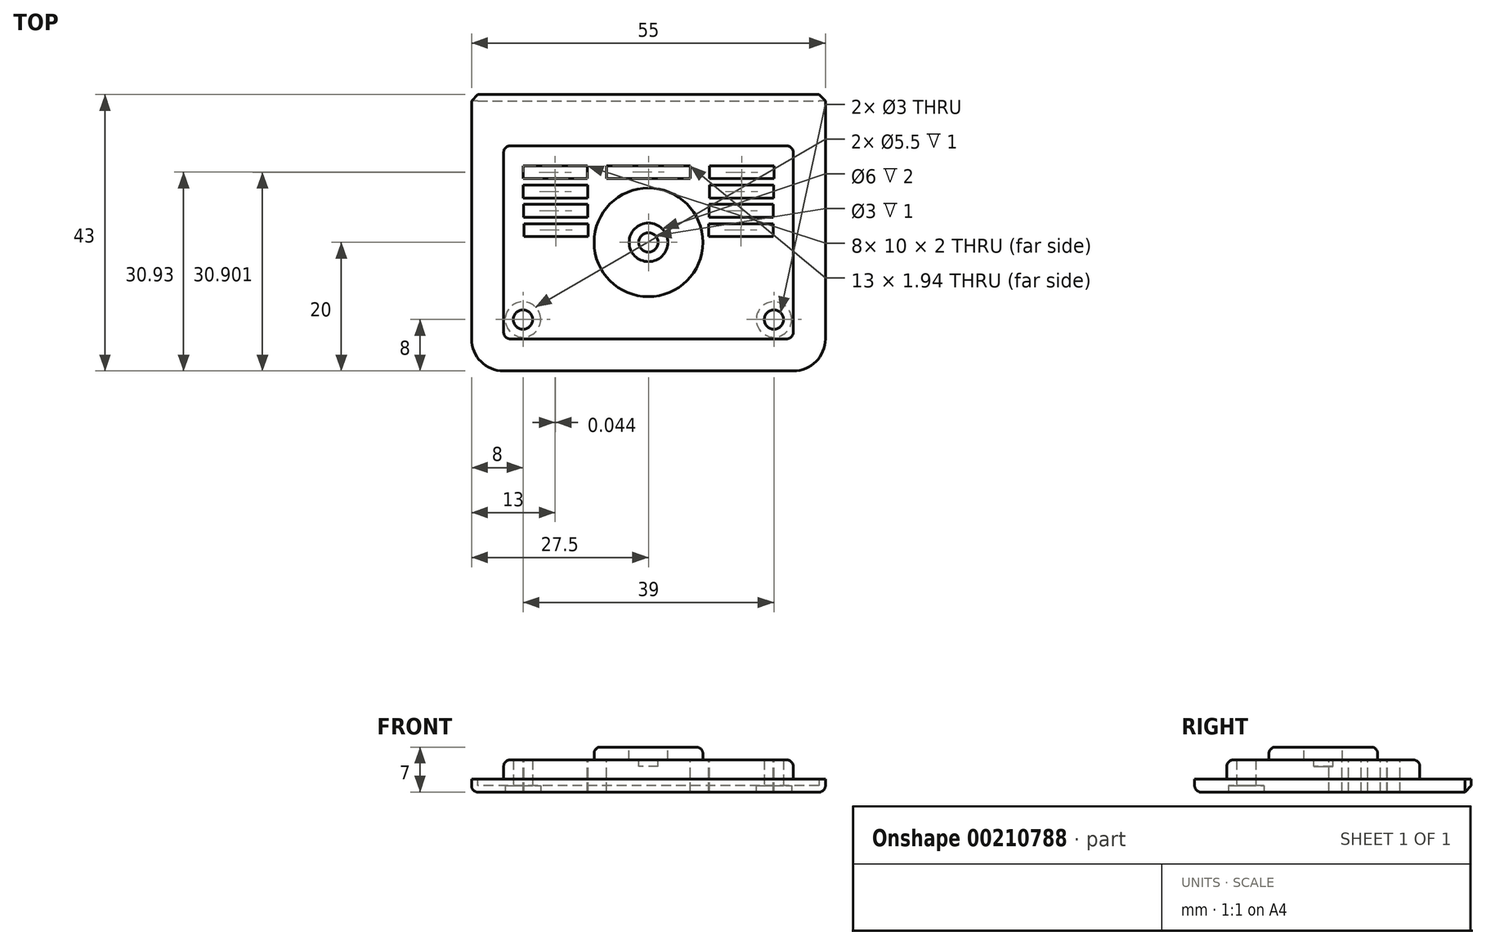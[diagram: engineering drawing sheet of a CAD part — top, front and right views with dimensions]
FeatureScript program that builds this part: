
annotation { "Feature Type Name" : "Feature", "Feature Type Description" : "" }
export const myFeature = defineFeature(function(context is Context, id is Id, definition is map)
    precondition{}
    {
        {
            var Q0;
            Q0=qCreatedBy(makeId("Top.planeOp"),FACE);
            var sketch = newSketch(context, id + "F0", { "sketchPlane" : qUnion([Q0])});
            skLineSegment(sketch, "E0.bottom", {"start": v(27.5, -20) * mm, "end": v(-27.5, -20) * mm});
            skLineSegment(sketch, "E0.top", {"start": v(27.5, 20) * mm, "end": v(-27.5, 20) * mm});
            skLineSegment(sketch, "E0.left", {"start": v(27.5, -20) * mm, "end": v(27.5, 20) * mm});
            skLineSegment(sketch, "E0.right", {"start": v(-27.5, -20) * mm, "end": v(-27.5, 20) * mm});
            skPoint(sketch, "E0.middle", {"position": v(0, 0) * mm});
            skSolve(sketch);
        }
        {
            var Q0;
            Q0 = qSketchRegion(id + "F0", true);
            extrude(context, id + "F1", {"entities" : qUnion([Q0]), "oppositeDirection" : true, "depth" : 2 * mm});
        }
        {
            var Q0;
            Q0=makeQuery(id+"F1.opExtrude","CAP_FACE",FACE,{"disambiguationData":[OSD([sQuery(id+"F0.wireOp",EDGE,"E0.bottom"),sQuery(id+"F0.wireOp",EDGE,"E0.top"),sQuery(id+"F0.wireOp",EDGE,"E0.left"),sQuery(id+"F0.wireOp",EDGE,"E0.right")])],"isStart":true});
            var sketch = newSketch(context, id + "F2", { "sketchPlane" : qUnion([Q0])});
            skLineSegment(sketch, "E1.bottom", {"start": v(-22.5, 15) * mm, "end": v(22.5, 15) * mm});
            skLineSegment(sketch, "E1.top", {"start": v(-22.5, -15) * mm, "end": v(22.5, -15) * mm});
            skLineSegment(sketch, "E1.left", {"start": v(-22.5, 15) * mm, "end": v(-22.5, -15) * mm});
            skLineSegment(sketch, "E1.right", {"start": v(22.5, 15) * mm, "end": v(22.5, -15) * mm});
            skSolve(sketch);
        }
        {
            var Q0;
            Q0 = qSketchRegion(id + "F2", true);
            extrude(context, id + "F3", {"entities" : qUnion([Q0]), "operationType" : NewBodyOperationType.ADD, "depth" : 3 * mm});
        }
        {
            var Q0;
            Q0=makeQuery(id+"F1.opExtrude","CAP_FACE",FACE,{"disambiguationData":[OSD([sQuery(id+"F0.wireOp",EDGE,"E0.bottom"),sQuery(id+"F0.wireOp",EDGE,"E0.top"),sQuery(id+"F0.wireOp",EDGE,"E0.left"),sQuery(id+"F0.wireOp",EDGE,"E0.right")])],"isStart":false});
            var sketch = newSketch(context, id + "F4", { "sketchPlane" : qUnion([Q0])});
            skCircle(sketch, "E2", {"center": v(19.5, 12) * mm, "radius": 1.5 * mm});
            skCircle(sketch, "E3", {"center": v(-19.5, 12) * mm, "radius": 1.5 * mm});
            skSolve(sketch);
        }
        {
            var Q0;
            Q0 = qSketchRegion(id + "F4", true);
            extrude(context, id + "F5", {"entities" : qUnion([Q0]), "operationType" : NewBodyOperationType.REMOVE, "oppositeDirection" : true, "depth" : 25 * mm});
        }
        {
            var Q0;
            Q0=makeQuery(id+"F3.opExtrude","CAP_FACE",FACE,{"disambiguationData":[OSD([sQuery(id+"F2.wireOp",EDGE,"E1.bottom"),sQuery(id+"F2.wireOp",EDGE,"E1.top"),sQuery(id+"F2.wireOp",EDGE,"E1.left"),sQuery(id+"F2.wireOp",EDGE,"E1.right")])],"isStart":false});
            var sketch = newSketch(context, id + "F6", { "sketchPlane" : qUnion([Q0])});
            skCircle(sketch, "E4", {"center": v(0, 0) * mm, "radius": 8.45 * mm});
            skSolve(sketch);
        }
        {
            var Q0;
            Q0=makeQuery(id+"F6.imprint","IMPRINT",FACE,{"disambiguationData":[TD([[makeQuery(id+"F6.imprint","IMPRINT",EDGE,{"derivedFrom":sQuery(id+"F6.wireOp",EDGE,"E4")}),1.0]])]});
            extrude(context, id + "F7", {"entities" : qUnion([Q0]), "operationType" : NewBodyOperationType.ADD, "depth" : 2 * mm});
        }
        {
            var Q0;
            Q0=makeQuery(id+"F7.opExtrude","CAP_FACE",FACE,{"disambiguationData":[OSD([sQuery(id+"F6.wireOp",EDGE,"E4")])],"isStart":false});
            var sketch = newSketch(context, id + "F8", { "sketchPlane" : qUnion([Q0])});
            skCircle(sketch, "E5", {"center": v(0, 0) * mm, "radius": 3 * mm});
            skSolve(sketch);
        }
        {
            var Q0;
            Q0=makeQuery(id+"F8.imprint","IMPRINT",FACE,{"disambiguationData":[TD([[makeQuery(id+"F8.imprint","IMPRINT",EDGE,{"derivedFrom":sQuery(id+"F8.wireOp",EDGE,"E5")}),1.0]])]});
            extrude(context, id + "F9", {"entities" : qUnion([Q0]), "operationType" : NewBodyOperationType.REMOVE, "oppositeDirection" : true, "depth" : 2 * mm});
        }
        {
            var Q0;
            Q0=makeQuery(id+"F9.boolean.opBoolean","COPY",FACE,{"derivedFrom":makeQuery(id+"F9.opExtrude","CAP_FACE",FACE,{"disambiguationData":[OSD([sQuery(id+"F8.wireOp",EDGE,"E5")])],"isStart":false})});
            var sketch = newSketch(context, id + "F10", { "sketchPlane" : qUnion([Q0])});
            skCircle(sketch, "E6", {"center": v(0, 0) * mm, "radius": 1.5 * mm});
            skSolve(sketch);
        }
        {
            var Q0;
            Q0 = qSketchRegion(id + "F10", true);
            extrude(context, id + "F11", {"entities" : qUnion([Q0]), "operationType" : NewBodyOperationType.REMOVE, "oppositeDirection" : true, "depth" : 1 * mm});
        }
        {
            var Q0;
            Q0=makeQuery(id+"F1.opExtrude","SWEPT_EDGE",EDGE,{"disambiguationData":[OSD([sQuery(id+"F0.wireOp",EDGE,"E0.bottom"),sQuery(id+"F0.wireOp",EDGE,"E0.right")])]});
            var Q1;
            Q1=makeQuery(id+"F1.opExtrude","SWEPT_EDGE",EDGE,{"disambiguationData":[OSD([sQuery(id+"F0.wireOp",EDGE,"E0.bottom"),sQuery(id+"F0.wireOp",EDGE,"E0.left")])]});
            fillet(context, id + "F12", {"entities" : qUnion([Q0, Q1]), "radius" : 5 * mm, "tangentPropagation" : true, "allowEdgeOverflow" : false});
        }
        {
            var Q0;
            Q0=makeQuery(id+"F3.opExtrude","SWEPT_EDGE",EDGE,{"disambiguationData":[OSD([sQuery(id+"F2.wireOp",EDGE,"E1.top"),sQuery(id+"F2.wireOp",EDGE,"E1.right")])]});
            var Q1;
            Q1=makeQuery(id+"F3.opExtrude","SWEPT_EDGE",EDGE,{"disambiguationData":[OSD([sQuery(id+"F2.wireOp",EDGE,"E1.top"),sQuery(id+"F2.wireOp",EDGE,"E1.left")])]});
            var Q2;
            Q2=makeQuery(id+"F3.opExtrude","SWEPT_EDGE",EDGE,{"disambiguationData":[OSD([sQuery(id+"F2.wireOp",EDGE,"E1.bottom"),sQuery(id+"F2.wireOp",EDGE,"E1.left")])]});
            var Q3;
            Q3=makeQuery(id+"F3.opExtrude","SWEPT_EDGE",EDGE,{"disambiguationData":[OSD([sQuery(id+"F2.wireOp",EDGE,"E1.bottom"),sQuery(id+"F2.wireOp",EDGE,"E1.right")])]});
            var Q4;
            Q4=makeQuery(id+"F3.opExtrude","CAP_EDGE",EDGE,{"disambiguationData":[OSD([sQuery(id+"F2.wireOp",EDGE,"E1.right")])],"isStart":false});
            var Q5;
            Q5=makeQuery(id+"F3.opExtrude","CAP_EDGE",EDGE,{"disambiguationData":[OSD([sQuery(id+"F2.wireOp",EDGE,"E1.bottom")])],"isStart":false});
            var Q6;
            Q6=makeQuery(id+"F3.opExtrude","CAP_EDGE",EDGE,{"disambiguationData":[OSD([sQuery(id+"F2.wireOp",EDGE,"E1.left")])],"isStart":false});
            var Q7;
            Q7=makeQuery(id+"F3.opExtrude","CAP_EDGE",EDGE,{"disambiguationData":[OSD([sQuery(id+"F2.wireOp",EDGE,"E1.top")])],"isStart":false});
            fillet(context, id + "F13", {"entities" : qUnion([Q0, Q1, Q2, Q3, Q4, Q5, Q6, Q7]), "radius" : 1 * mm, "tangentPropagation" : true, "allowEdgeOverflow" : false});
        }
        {
            var Q0;
            Q0=makeQuery(id+"F7.opExtrude","CAP_EDGE",EDGE,{"disambiguationData":[OSD([sQuery(id+"F6.wireOp",EDGE,"E4")])],"isStart":false});
            var Q1;
            Q1=makeQuery(id+"F1.opExtrude","CAP_EDGE",EDGE,{"disambiguationData":[OSD([sQuery(id+"F0.wireOp",EDGE,"E0.bottom")])],"isStart":false});
            fillet(context, id + "F14", {"entities" : qUnion([Q0, Q1]), "radius" : 1 * mm, "tangentPropagation" : true, "allowEdgeOverflow" : false});
        }
        {
            var Q0;
            Q0=makeQuery(id+"F3.opExtrude","CAP_FACE",FACE,{"disambiguationData":[OSD([sQuery(id+"F2.wireOp",EDGE,"E1.bottom"),sQuery(id+"F2.wireOp",EDGE,"E1.top"),sQuery(id+"F2.wireOp",EDGE,"E1.left"),sQuery(id+"F2.wireOp",EDGE,"E1.right")])],"isStart":false});
            var sketch = newSketch(context, id + "F15", { "sketchPlane" : qUnion([Q0])});
            skLineSegment(sketch, "E7.1.0.0", {"start": v(19.5, 11.9) * mm, "end": v(19.5, 9.9) * mm});
            skLineSegment(sketch, "E7.1.0.1", {"start": v(9.5, 11.9) * mm, "end": v(9.5, 9.9) * mm});
            skLineSegment(sketch, "E7.1.0.2", {"start": v(9.5, 9.9) * mm, "end": v(19.5, 9.9) * mm});
            skLineSegment(sketch, "E7.1.0.3", {"start": v(9.5, 11.9) * mm, "end": v(19.5, 11.9) * mm});
            skLineSegment(sketch, "E7.1.1.0", {"start": v(19.46, 8.9) * mm, "end": v(19.46, 6.9) * mm});
            skLineSegment(sketch, "E7.1.1.1", {"start": v(9.46, 8.9) * mm, "end": v(9.46, 6.9) * mm});
            skLineSegment(sketch, "E7.1.1.2", {"start": v(9.46, 6.9) * mm, "end": v(19.46, 6.9) * mm});
            skLineSegment(sketch, "E7.1.1.3", {"start": v(9.46, 8.9) * mm, "end": v(19.46, 8.9) * mm});
            skLineSegment(sketch, "E7.1.2.0", {"start": v(19.41, 5.9) * mm, "end": v(19.41, 3.9) * mm});
            skLineSegment(sketch, "E7.1.2.1", {"start": v(9.41, 5.9) * mm, "end": v(9.41, 3.9) * mm});
            skLineSegment(sketch, "E7.1.2.2", {"start": v(9.41, 3.9) * mm, "end": v(19.41, 3.9) * mm});
            skLineSegment(sketch, "E7.1.2.3", {"start": v(9.41, 5.9) * mm, "end": v(19.41, 5.9) * mm});
            skLineSegment(sketch, "E7.1.3.0", {"start": v(19.37, 2.9) * mm, "end": v(19.37, 0.9) * mm});
            skLineSegment(sketch, "E7.1.3.1", {"start": v(9.37, 2.9) * mm, "end": v(9.37, 0.9) * mm});
            skLineSegment(sketch, "E7.1.3.2", {"start": v(9.37, 0.9) * mm, "end": v(19.37, 0.9) * mm});
            skLineSegment(sketch, "E7.1.3.3", {"start": v(9.37, 2.9) * mm, "end": v(19.37, 2.9) * mm});
            skLineSegment(sketch, "E7.direction1", {"start": v(-19.5, 10) * mm, "end": v(9.5, 9.9) * mm, "construction": true});
            skLineSegment(sketch, "E8.MirrorCS", {"start": v(-9.5, 9.9) * mm, "end": v(-19.5, 9.9) * mm});
            skLineSegment(sketch, "E9.MirrorCS", {"start": v(-9.37, 2.9) * mm, "end": v(-9.37, 0.9) * mm});
            skLineSegment(sketch, "E10.MirrorCS", {"start": v(-19.46, 8.9) * mm, "end": v(-19.46, 6.9) * mm});
            skLineSegment(sketch, "E11.MirrorCS", {"start": v(-9.37, 2.9) * mm, "end": v(-19.37, 2.9) * mm});
            skLineSegment(sketch, "E12.MirrorCS", {"start": v(-9.46, 8.9) * mm, "end": v(-19.46, 8.9) * mm});
            skLineSegment(sketch, "E13.MirrorCS", {"start": v(-9.41, 3.9) * mm, "end": v(-19.41, 3.9) * mm});
            skLineSegment(sketch, "E14.MirrorCS", {"start": v(-9.41, 5.9) * mm, "end": v(-9.41, 3.9) * mm});
            skLineSegment(sketch, "E15.MirrorCS", {"start": v(-9.5, 11.9) * mm, "end": v(-9.5, 9.9) * mm});
            skLineSegment(sketch, "E16.MirrorCS", {"start": v(-9.46, 6.9) * mm, "end": v(-19.46, 6.9) * mm});
            skLineSegment(sketch, "E17.MirrorCS", {"start": v(-9.41, 5.9) * mm, "end": v(-19.41, 5.9) * mm});
            skLineSegment(sketch, "E18.MirrorCS", {"start": v(-19.5, 11.9) * mm, "end": v(-19.5, 9.9) * mm});
            skLineSegment(sketch, "E19.MirrorCS", {"start": v(-9.37, 0.9) * mm, "end": v(-19.37, 0.9) * mm});
            skLineSegment(sketch, "E20.MirrorCS", {"start": v(-19.37, 2.9) * mm, "end": v(-19.37, 0.9) * mm});
            skLineSegment(sketch, "E21.MirrorCS", {"start": v(-9.5, 11.9) * mm, "end": v(-19.5, 11.9) * mm});
            skLineSegment(sketch, "E22.MirrorCS", {"start": v(-19.41, 5.9) * mm, "end": v(-19.41, 3.9) * mm});
            skLineSegment(sketch, "E23.MirrorCS", {"start": v(-9.46, 8.9) * mm, "end": v(-9.46, 6.9) * mm});
            skLineSegment(sketch, "E24.bottom", {"start": v(-6.5, 9.96) * mm, "end": v(6.5, 9.96) * mm});
            skLineSegment(sketch, "E24.top", {"start": v(-6.5, 11.9) * mm, "end": v(6.5, 11.9) * mm});
            skLineSegment(sketch, "E24.left", {"start": v(-6.5, 9.96) * mm, "end": v(-6.5, 11.9) * mm});
            skLineSegment(sketch, "E24.right", {"start": v(6.5, 9.96) * mm, "end": v(6.5, 11.9) * mm});
            skSolve(sketch);
        }
        {
            var Q0;
            Q0 = qSketchRegion(id + "F15", true);
            extrude(context, id + "F16", {"entities" : qUnion([Q0]), "operationType" : NewBodyOperationType.REMOVE, "endBound" : BoundingType.THROUGH_ALL, "oppositeDirection" : true, "depth" : 25 * mm});
        }
        {
            var Q0;
            Q0=makeQuery(id+"F1.opExtrude","SWEPT_FACE",FACE,{"disambiguationData":[OSD([sQuery(id+"F0.wireOp",EDGE,"E0.top")])]});
            extrude(context, id + "F17", {"entities" : qUnion([Q0]), "operationType" : NewBodyOperationType.ADD, "depth" : 3 * mm});
        }
        {
            var Q0;
            {var subQ0=sQuery(id+"F0.wireOp",EDGE,"E0.top");Q0=makeQuery(id+"F17.opExtrude","CAP_EDGE",EDGE,{"disambiguationData":[OSD([subQ0]),TDD([makeQuery(id+"F1.opExtrude","CAP_EDGE",EDGE,{"disambiguationData":[OSD([subQ0])],"isStart":false})])],"isStart":false});}
            chamfer(context, id + "F18", {"entities" : qUnion([Q0]), "width" : 1 * mm, "tangentPropagation" : true});
        }
        {
            var Q0;
            {var subQ0=sQuery(id+"F0.wireOp",EDGE,"E0.top");Q0=makeQuery(id+"F17.boolean.opBoolean","MERGE",FACE,{"derivedFrom":[makeQuery(id+"F1.opExtrude","CAP_FACE",FACE,{"disambiguationData":[OSD([sQuery(id+"F0.wireOp",EDGE,"E0.bottom"),subQ0,sQuery(id+"F0.wireOp",EDGE,"E0.left"),sQuery(id+"F0.wireOp",EDGE,"E0.right")])],"isStart":false}),makeQuery(id+"F17.opExtrude","SWEPT_FACE",FACE,{"disambiguationData":[OSD([subQ0]),TDD([makeQuery(id+"F1.opExtrude","CAP_EDGE",EDGE,{"disambiguationData":[OSD([subQ0])],"isStart":false})])]})]});}
            var sketch = newSketch(context, id + "F19", { "sketchPlane" : qUnion([Q0])});
            skCircle(sketch, "E25", {"center": v(-19.5, 12) * mm, "radius": 2.75 * mm});
            skCircle(sketch, "E26", {"center": v(19.5, 12) * mm, "radius": 2.75 * mm});
            skSolve(sketch);
        }
        {
            var Q0;
            Q0 = qSketchRegion(id + "F19", true);
            extrude(context, id + "F20", {"entities" : qUnion([Q0]), "operationType" : NewBodyOperationType.REMOVE, "oppositeDirection" : true, "depth" : 1 * mm});
        }
    });
